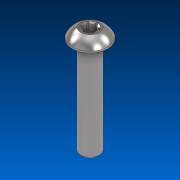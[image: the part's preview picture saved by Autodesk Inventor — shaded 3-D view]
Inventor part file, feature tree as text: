
AUTODESK INVENTOR PART (.ipt)
format: ipt  version: 2022.2 (Build 262287000, 287)  size: 176,640 bytes
history: native  units: in
note: dims shown in document units (in); Inventor stores cm internally (conversion verified against a paired STEP export)
features: direct_edit x1, chamfer x1, move_body x1
ambient origin geometry x8: Origin, YZ Plane, XZ Plane, XY Plane, X Axis, Y Axis, Z Axis, Center Point
bodies: Solid1 (feature_tree)
feature tree (3):
  direct_edit  "Direct Edit1"
  chamfer  "Chamfer2"  [1 undecoded]
  move_body  "Move1"
note: 1 required parameter value undecoded (feature->parameter linkage not recoverable at this tier; creation-order binding heuristic only, values carry confidence <= 0.55)
